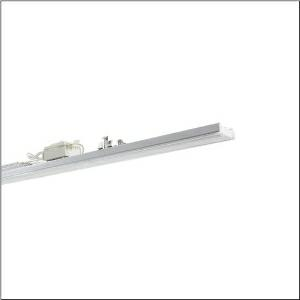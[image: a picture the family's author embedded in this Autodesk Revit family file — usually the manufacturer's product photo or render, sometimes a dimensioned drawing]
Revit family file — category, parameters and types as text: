
# Revit family: licross_r__11_recessed_mo_51tl18dn495g_dc76
name_source: partatom
category: Lighting Fixtures
units: mm (PartAtom-declared; Revit-internal decimal feet)

## family parameters
Cut with Voids When Loaded = No
Host = Face
Light Source = No
Part Type = Normal
Room Calculation Point = No
Round Connector Dimension = Use Diameter
Shared = No

## types (1)
- --- (1 x LED, 9950 lm, 56.7 W, 4000K)
    Apparent Load = 57 VA
    CIE Flux Codes = 83 96 99 100 100
    Color Rendering = 80
    Color Temperature = 4000K
    Default Elevation = 1800 mm
    Description = Licross® 11 Recessed MO, luminaire insert, of sheet steel, coil coated, white, length: 1.500mm, width: 66mm, height: 67mm, LED rated luminous flux: 9.950lm, light colour: 840, control gear: DALI 2, with plug, 5-pole, with phase selection, mains connection: 220..240V, AC, 50/60Hz, rated input power: 57W, halogen-free wiring, primary light control with lens, of plastic, primary optical cover: cover, of PMMA, light emission: direct distribution, primary light characteristic: symmetric, protection rating (complete): IP40, insulation class (complete): insulation class I (protective earthing), certification: CE, ENEC, VDE, UKCA, protection symbol: D if used in an environment without relevant dust loads with corresponding accessories, impact resistance: IK06, permissible ambient temperature for indoor applications: -25..+35°C, corresponds to IFS (International Featured Standards) requirements for safety and quality in the food industry, reducing of maximum allowable ambient temperature of 5°C with ceiling mounting, LABS conformity tested according to VDMA 24364:2018-05, packaging unit: 1 piece
    Height = 58 mm
    Lamp = 1 x LED
    Lamp Light Flux = 9950 lm
    Lamp Power = 56.7 W
    Lamp count = 1
    Length = 1500 mm
    Luminous efficacy = 175 lm/W
    Manufacturer = Siteco
    ModVariant = No
    Model = 51TL18DN495G
    Mounting Place = Ceiling
    Mounting Type = Pendant
    Number of Poles = 1
    OnlyDefault = Yes
    Power Factor = 1
    Product Name = Licross® 11 Recessed MO
    Product group = luminaire insert
    ProductGroupID = 902
    Protection Class = Protection class I
    Protection Degree = IP 40
    RLX_Detail_Level = 1
    RLX_Emergency_Light_Flux = 0 lm
    RLX_Emergency_Type = 0
    RLX_Emergency_Type_DB = No
    RlxData = <blob elided: 24461 chars, md5=b45d2ec2>
    Socket = socket
    Standby Power = 0 W
    System Light Flux = 9950 lm
    System Power = 57 W
    Type Comments = factory setting: luminous flux: 100 % | dim-lin: 254 | 378 mA
    Type Image = l_1296930.jpg
    URL = http://relux.com
    VarID = @adj_099196
    Voltage = 0 V
    Weight = 0.00 kg
    Width = 66 mm

## geometry (parser evidence)
native form markers: Blend x4, Sweep x12
no freeform markers — native parametric forms only
